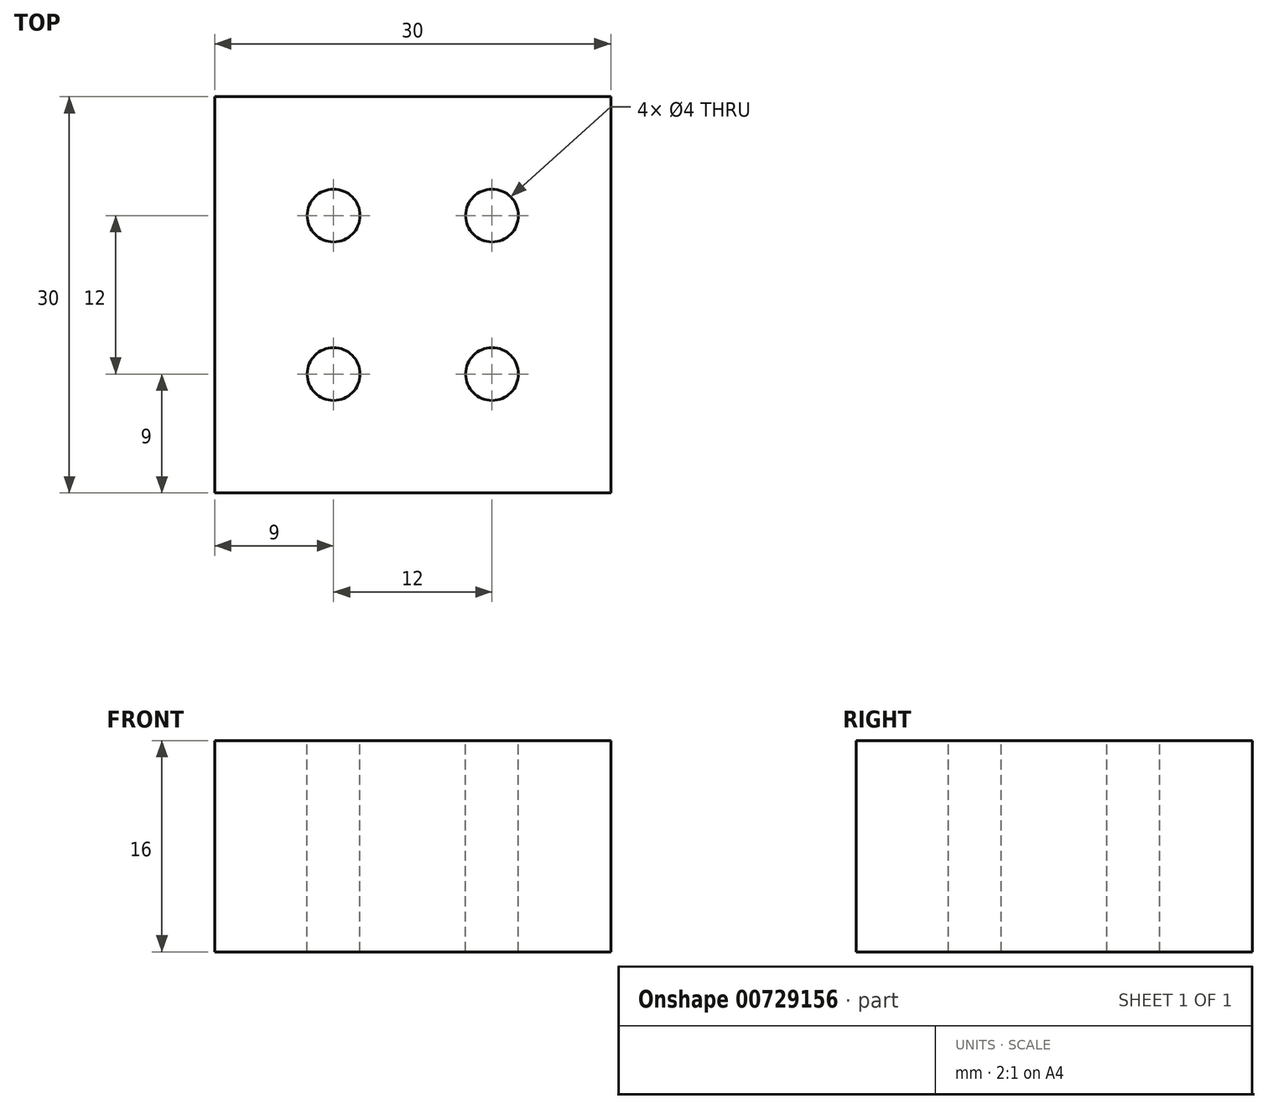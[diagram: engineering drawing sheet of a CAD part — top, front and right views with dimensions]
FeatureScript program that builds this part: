
annotation { "Feature Type Name" : "Feature", "Feature Type Description" : "" }
export const myFeature = defineFeature(function(context is Context, id is Id, definition is map)
    precondition{}
    {
        {
            var Q0;
            Q0=qCreatedBy(makeId("Top.planeOp"),FACE);
            var sketch = newSketch(context, id + "F0", { "sketchPlane" : qUnion([Q0])});
            skLineSegment(sketch, "E0.bottom", {"start": v(15, -15) * mm, "end": v(-15, -15) * mm});
            skLineSegment(sketch, "E0.top", {"start": v(15, 15) * mm, "end": v(-15, 15) * mm});
            skLineSegment(sketch, "E0.left", {"start": v(15, -15) * mm, "end": v(15, 15) * mm});
            skLineSegment(sketch, "E0.right", {"start": v(-15, -15) * mm, "end": v(-15, 15) * mm});
            skPoint(sketch, "E0.middle", {"position": v(0, 0) * mm});
            skSolve(sketch);
        }
        {
            var Q0;
            Q0=makeQuery(id+"F0.imprint","IMPRINT",FACE,{"disambiguationData":[TD([[makeQuery(id+"F0.imprint","IMPRINT",EDGE,{"derivedFrom":sQuery(id+"F0.wireOp",EDGE,"E0.bottom")}),-1.0]])]});
            extrude(context, id + "F1", {"entities" : qUnion([Q0]), "depth" : 16 * mm, "offsetDistance" : 25 * mm});
        }
        {
            var Q0;
            Q0=makeQuery(id+"F1.opExtrude","CAP_FACE",FACE,{"disambiguationData":[OSD([sQuery(id+"F0.wireOp",EDGE,"E0.bottom"),sQuery(id+"F0.wireOp",EDGE,"E0.top"),sQuery(id+"F0.wireOp",EDGE,"E0.left"),sQuery(id+"F0.wireOp",EDGE,"E0.right")])],"isStart":false});
            var sketch = newSketch(context, id + "F2", { "sketchPlane" : qUnion([Q0])});
            skPoint(sketch, "E1", {"position": v(6, -6) * mm});
            skPoint(sketch, "E2", {"position": v(-6, 6) * mm});
            skPoint(sketch, "E3", {"position": v(6, 6) * mm});
            skPoint(sketch, "E4", {"position": v(-6, -6) * mm});
            skLineSegment(sketch, "E5.bottom", {"start": v(6, -6) * mm, "end": v(-6, -6) * mm});
            skLineSegment(sketch, "E5.top", {"start": v(6, 6) * mm, "end": v(-6, 6) * mm});
            skLineSegment(sketch, "E5.left", {"start": v(6, -6) * mm, "end": v(6, 6) * mm});
            skLineSegment(sketch, "E5.right", {"start": v(-6, -6) * mm, "end": v(-6, 6) * mm});
            skSolve(sketch);
        }
        {
            var Q0;
            Q0=sQuery(id+"F2.wireOp",VERTEX,"E1");
            var Q1;
            Q1=sQuery(id+"F2.wireOp",VERTEX,"E4");
            var Q2;
            Q2=sQuery(id+"F2.wireOp",VERTEX,"E2");
            var Q3;
            Q3=sQuery(id+"F2.wireOp",VERTEX,"E3");
            var Q4;
            Q4=makeQuery(id+"F1.opExtrude","SWEPT_BODY",BODY,{"disambiguationData":[OSD([sQuery(id+"F0.wireOp",EDGE,"E0.bottom"),sQuery(id+"F0.wireOp",EDGE,"E0.top"),sQuery(id+"F0.wireOp",EDGE,"E0.left"),sQuery(id+"F0.wireOp",EDGE,"E0.right")])]});
            hole(context, id + "F3", {"style" : HoleStyle.SIMPLE, "endStyle" : HoleEndStyle.THROUGH, "holeDiameter" : 4 * mm, "majorDiameter" : 5 * mm, "isTappedThrough" : true, "tappedDepth" : 12 * mm, "tapClearance" : 3, "locations" : qUnion([Q0, Q1, Q2, Q3]), "scope" : qUnion([Q4])});
        }
    });
